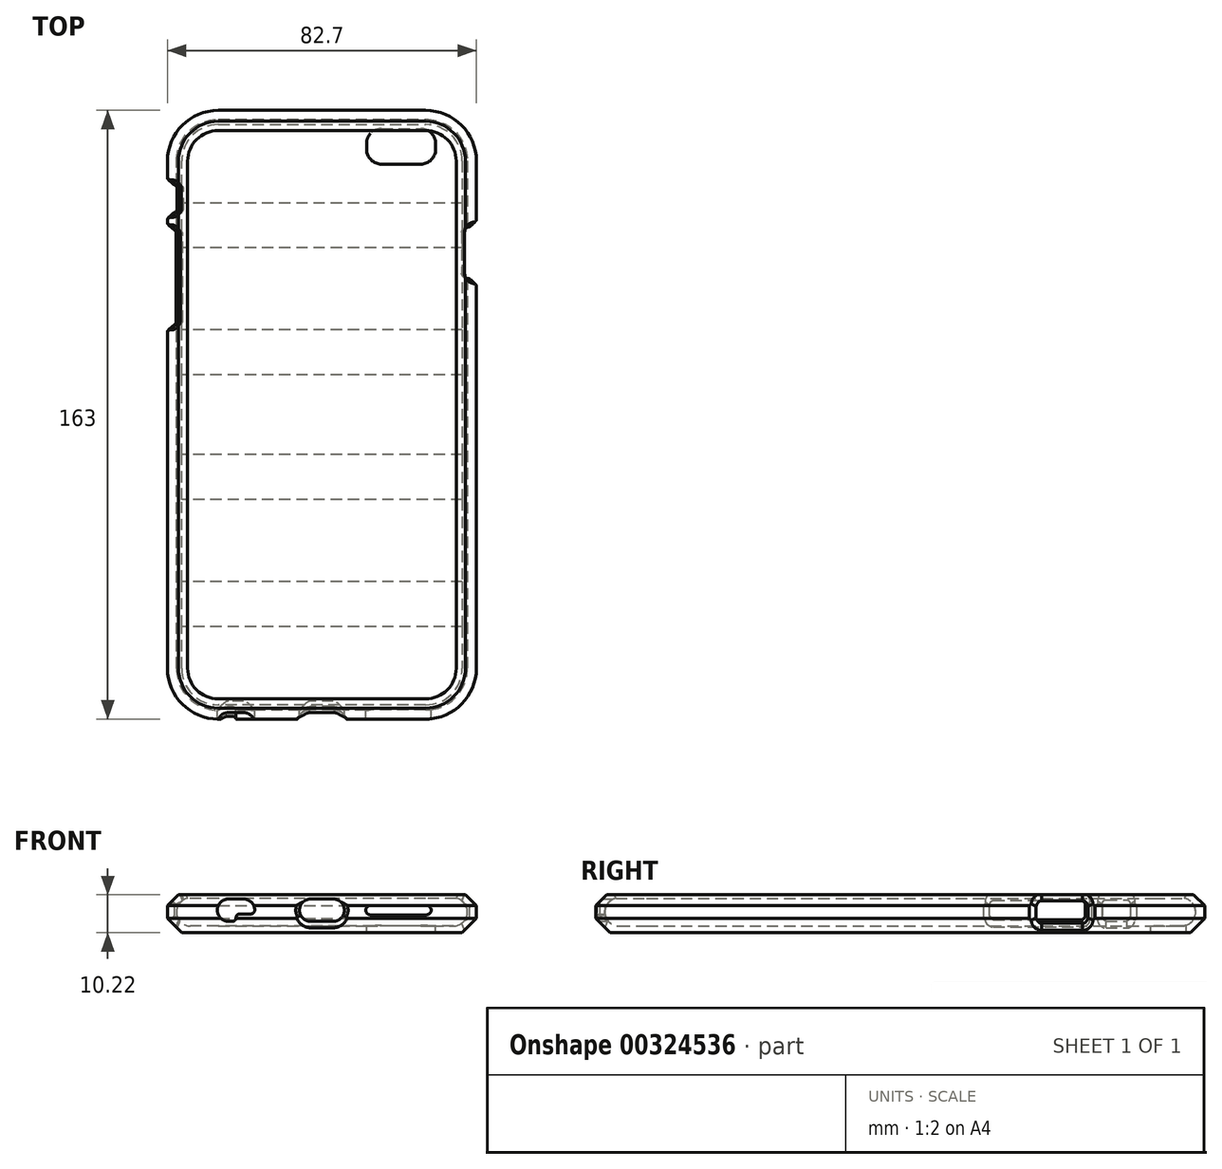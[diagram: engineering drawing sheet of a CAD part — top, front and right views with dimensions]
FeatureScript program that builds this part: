
annotation { "Feature Type Name" : "Feature", "Feature Type Description" : "" }
export const myFeature = defineFeature(function(context is Context, id is Id, definition is map)
    precondition{}
    {
        {
            assignVariable(context, id + "F0", {"name" : "HoleChamferLength", "anyValue" : 1.25});
        }
        {
            assignVariable(context, id + "F1", {"name" : "HoleChamferTopBottom", "anyValue" : 1.75});
        }
        {
            var Q0;
            Q0=qCreatedBy(makeId("Top.planeOp"),FACE);
            var sketch = newSketch(context, id + "F2", { "sketchPlane" : qUnion([Q0])});
            skLineSegment(sketch, "E0.bottom", {"start": v(27.75, 79.1) * mm, "end": v(0, 79.1) * mm});
            skLineSegment(sketch, "E0.top", {"start": v(27.75, -79.1) * mm, "end": v(-27.75, -79.1) * mm});
            skLineSegment(sketch, "E0.left", {"start": v(38.95, 67.9) * mm, "end": v(38.95, -67.9) * mm});
            skLineSegment(sketch, "E0.right", {"start": v(-38.95, 67.9) * mm, "end": v(-38.95, -67.9) * mm});
            skPoint(sketch, "E0.middle", {"position": v(0, 0) * mm});
            skPoint(sketch, "E1.visualSharp", {"position": v(-38.95, 79.1) * mm});
            skArc(sketch, "E1.filletArc", {"start": v(-27.75, 79.1) * mm, "mid": v(-35.67, 75.82) * mm, "end": v(-38.95, 67.9) * mm});
            skPoint(sketch, "E2.visualSharp", {"position": v(38.95, 79.1) * mm});
            skArc(sketch, "E2.filletArc", {"start": v(38.95, 67.9) * mm, "mid": v(35.67, 75.82) * mm, "end": v(27.75, 79.1) * mm});
            skPoint(sketch, "E3.visualSharp", {"position": v(38.95, -79.1) * mm});
            skArc(sketch, "E3.filletArc", {"start": v(27.75, -79.1) * mm, "mid": v(35.67, -75.82) * mm, "end": v(38.95, -67.9) * mm});
            skPoint(sketch, "E4.visualSharp", {"position": v(-38.95, -79.1) * mm});
            skArc(sketch, "E4.filletArc", {"start": v(-38.95, -67.9) * mm, "mid": v(-35.67, -75.82) * mm, "end": v(-27.75, -79.1) * mm});
            skLineSegment(sketch, "E5", {"start": v(0, 79.1) * mm, "end": v(-27.75, 79.1) * mm});
            skSolve(sketch);
        }
        {
            var Q0;
            Q0=qCreatedBy(makeId("Right.planeOp"),FACE);
            var sketch = newSketch(context, id + "F3", { "sketchPlane" : qUnion([Q0])});
            skPoint(sketch, "E6.0", {"position": v(79.1, 0) * mm});
            skArc(sketch, "E7", {"start": v(75.35, -3.75) * mm, "mid": v(79.1, 0) * mm, "end": v(75.35, 3.75) * mm});
            skLineSegment(sketch, "E8", {"start": v(75.35, -3.75) * mm, "end": v(75.35, 3.75) * mm, "construction": true});
            skLineSegment(sketch, "E9", {"start": v(81.5, -1.75) * mm, "end": v(81.5, 1.75) * mm});
            skLineSegment(sketch, "E10", {"start": v(81.5, 1.75) * mm, "end": v(79.75, 3.5) * mm});
            skLineSegment(sketch, "E11.trimOffspring", {"start": v(79.75, -3.5) * mm, "end": v(81.5, -1.75) * mm});
            skLineSegment(sketch, "E12", {"start": v(75.35, -5.55) * mm, "end": v(75.35, -3.75) * mm});
            skLineSegment(sketch, "E13", {"start": v(75.35, -5.55) * mm, "end": v(84.8, -5.55) * mm, "construction": true});
            skPoint(sketch, "E14", {"position": v(81.5, 0) * mm});
            skPoint(sketch, "E15.visualSharp", {"position": v(66.64, 4.7) * mm});
            skArc(sketch, "E15.filletArc", {"start": v(77.32, 4.67) * mm, "mid": v(76.53, 4.4) * mm, "end": v(76.1, 3.67) * mm});
            skLineSegment(sketch, "E16", {"start": v(79.75, -3.5) * mm, "end": v(77.7, -5.55) * mm});
            skLineSegment(sketch, "E17", {"start": v(77.7, -5.55) * mm, "end": v(75.35, -5.55) * mm});
            skLineSegment(sketch, "E18", {"start": v(79.75, 3.5) * mm, "end": v(78.58, 4.67) * mm});
            skLineSegment(sketch, "E19", {"start": v(78.58, 4.67) * mm, "end": v(77.32, 4.67) * mm});
            skLineSegment(sketch, "E20", {"start": v(76.1, 3.67) * mm, "end": v(66.64, 5.6) * mm, "construction": true});
            skSolve(sketch);
        }
        {
            var Q0;
            Q0=sQuery(id+"F2.wireOp",EDGE,"E5");
            var Q1;
            Q1=sQuery(id+"F2.wireOp",VERTEX,"E5.end");
            cPlane(context, id + "F4", {"entities" : qUnion([Q0, Q1]), "cplaneType" : CPlaneType.LINE_POINT, "offset" : 25 * mm, "width" : 150 * mm, "height" : 150 * mm});
        }
        {
            var Q0;
            Q0=sQuery(id+"F2.wireOp",EDGE,"E0.bottom");
            var Q1;
            Q1=sQuery(id+"F2.wireOp",VERTEX,"E2.filletArc.end");
            cPlane(context, id + "F5", {"entities" : qUnion([Q0, Q1]), "cplaneType" : CPlaneType.LINE_POINT, "offset" : 25 * mm, "width" : 150 * mm, "height" : 150 * mm});
        }
        {
            var Q0;
            Q0=sQuery(id+"F2.wireOp",EDGE,"E0.right");
            var Q1;
            Q1=sQuery(id+"F2.wireOp",VERTEX,"E0.right.end");
            cPlane(context, id + "F6", {"entities" : qUnion([Q0, Q1]), "cplaneType" : CPlaneType.LINE_POINT, "offset" : 25 * mm, "width" : 150 * mm, "height" : 150 * mm});
        }
        {
            var Q0;
            Q0=qCreatedBy(id+"F4.planeOp",FACE);
            var sketch = newSketch(context, id + "F7", { "sketchPlane" : qUnion([Q0])});
            skLineSegment(sketch, "E21.bottom", {"start": v(-24.95, -1.88) * mm, "end": v(-48.6, -1.88) * mm});
            skLineSegment(sketch, "E21.top", {"start": v(-24.95, 2.87) * mm, "end": v(-48.6, 2.87) * mm});
            skLineSegment(sketch, "E21.left", {"start": v(-23.95, -0.88) * mm, "end": v(-23.95, 1.87) * mm});
            skLineSegment(sketch, "E21.right", {"start": v(-49.6, -0.88) * mm, "end": v(-49.6, 1.87) * mm});
            skPoint(sketch, "E21.middle", {"position": v(-36.77, 0.5) * mm});
            skPoint(sketch, "E22.visualSharp", {"position": v(-49.6, 2.87) * mm});
            skArc(sketch, "E22.filletArc", {"start": v(-48.6, 2.87) * mm, "mid": v(-49.3, 2.58) * mm, "end": v(-49.6, 1.87) * mm});
            skPoint(sketch, "E23.visualSharp", {"position": v(-49.6, -1.88) * mm});
            skArc(sketch, "E23.filletArc", {"start": v(-49.6, -0.88) * mm, "mid": v(-49.3, -1.58) * mm, "end": v(-48.6, -1.88) * mm});
            skPoint(sketch, "E24.visualSharp", {"position": v(-23.95, 2.87) * mm});
            skArc(sketch, "E24.filletArc", {"start": v(-23.95, 1.87) * mm, "mid": v(-24.24, 2.58) * mm, "end": v(-24.95, 2.87) * mm});
            skPoint(sketch, "E25.visualSharp", {"position": v(-23.95, -1.88) * mm});
            skArc(sketch, "E25.filletArc", {"start": v(-24.95, -1.88) * mm, "mid": v(-24.24, -1.58) * mm, "end": v(-23.95, -0.88) * mm});
            skLineSegment(sketch, "E26.bottom", {"start": v(-60.6, 3.12) * mm, "end": v(-55.1, 3.12) * mm});
            skLineSegment(sketch, "E26.top", {"start": v(-60.6, -2.13) * mm, "end": v(-55.1, -2.13) * mm});
            skLineSegment(sketch, "E26.left", {"start": v(-61.6, 2.12) * mm, "end": v(-61.6, -1.13) * mm});
            skLineSegment(sketch, "E26.right", {"start": v(-54.1, 2.12) * mm, "end": v(-54.1, -1.13) * mm});
            skPoint(sketch, "E26.middle", {"position": v(-57.85, 0.5) * mm});
            skPoint(sketch, "E27.visualSharp", {"position": v(-61.6, 3.12) * mm});
            skArc(sketch, "E27.filletArc", {"start": v(-60.6, 3.13) * mm, "mid": v(-61.3, 2.83) * mm, "end": v(-61.6, 2.12) * mm});
            skPoint(sketch, "E28.visualSharp", {"position": v(-61.6, -2.13) * mm});
            skArc(sketch, "E28.filletArc", {"start": v(-61.6, -1.13) * mm, "mid": v(-61.3, -1.83) * mm, "end": v(-60.6, -2.13) * mm});
            skPoint(sketch, "E29.visualSharp", {"position": v(-54.1, -2.13) * mm});
            skArc(sketch, "E29.filletArc", {"start": v(-55.1, -2.13) * mm, "mid": v(-54.4, -1.83) * mm, "end": v(-54.1, -1.13) * mm});
            skPoint(sketch, "E30.visualSharp", {"position": v(-54.1, 3.12) * mm});
            skArc(sketch, "E30.filletArc", {"start": v(-54.1, 2.12) * mm, "mid": v(-54.4, 2.83) * mm, "end": v(-55.1, 3.13) * mm});
            skSolve(sketch);
        }
        {
            var Q0;
            Q0=qCreatedBy(id+"F5.planeOp",FACE);
            var sketch = newSketch(context, id + "F8", { "sketchPlane" : qUnion([Q0])});
            skLineSegment(sketch, "E31.bottom", {"start": v(-48.85, 2.75) * mm, "end": v(-37.85, 2.75) * mm});
            skLineSegment(sketch, "E31.top", {"start": v(-48.85, -2.75) * mm, "end": v(-37.85, -2.75) * mm});
            skLineSegment(sketch, "E31.left", {"start": v(-50.35, 1.25) * mm, "end": v(-50.35, -1.25) * mm});
            skLineSegment(sketch, "E31.right", {"start": v(-36.35, 1.25) * mm, "end": v(-36.35, -1.25) * mm});
            skPoint(sketch, "E31.middle", {"position": v(-43.35, 0) * mm});
            skPoint(sketch, "E32.visualSharp", {"position": v(-50.35, 2.75) * mm});
            skArc(sketch, "E32.filletArc", {"start": v(-48.85, 2.75) * mm, "mid": v(-49.91, 2.31) * mm, "end": v(-50.35, 1.25) * mm});
            skPoint(sketch, "E33.visualSharp", {"position": v(-50.35, -2.75) * mm});
            skArc(sketch, "E33.filletArc", {"start": v(-50.35, -1.25) * mm, "mid": v(-49.91, -2.31) * mm, "end": v(-48.85, -2.75) * mm});
            skPoint(sketch, "E34.visualSharp", {"position": v(-36.35, -2.75) * mm});
            skArc(sketch, "E34.filletArc", {"start": v(-37.85, -2.75) * mm, "mid": v(-36.79, -2.31) * mm, "end": v(-36.35, -1.25) * mm});
            skPoint(sketch, "E35.visualSharp", {"position": v(-36.35, 2.75) * mm});
            skArc(sketch, "E35.filletArc", {"start": v(-36.35, 1.25) * mm, "mid": v(-36.79, 2.31) * mm, "end": v(-37.85, 2.75) * mm});
            skSolve(sketch);
        }
        {
            var Q0;
            Q0=qCreatedBy(id+"F6.planeOp",FACE);
            var sketch = newSketch(context, id + "F9", { "sketchPlane" : qUnion([Q0])});
            skLineSegment(sketch, "E36.bottom", {"start": v(3, 3.5) * mm, "end": v(-3, 3.5) * mm});
            skLineSegment(sketch, "E36.top", {"start": v(3, -2.5) * mm, "end": v(-3, -2.5) * mm});
            skLineSegment(sketch, "E36.left", {"start": v(6, 0.5) * mm, "end": v(6, 0.5) * mm});
            skLineSegment(sketch, "E36.right", {"start": v(-6, 0.5) * mm, "end": v(-6, 0.5) * mm});
            skPoint(sketch, "E36.middle", {"position": v(0, 0.5) * mm});
            skArc(sketch, "E37", {"start": v(-25, 3.5) * mm, "mid": v(-28, 0.5) * mm, "end": v(-25, -2.5) * mm});
            skPoint(sketch, "E38.visualSharp", {"position": v(-6, 3.5) * mm});
            skArc(sketch, "E38.filletArc", {"start": v(-3, 3.5) * mm, "mid": v(-5.12, 2.62) * mm, "end": v(-6, 0.5) * mm});
            skPoint(sketch, "E39.visualSharp", {"position": v(-6, -2.5) * mm});
            skArc(sketch, "E39.filletArc", {"start": v(-6, 0.5) * mm, "mid": v(-5.12, -1.62) * mm, "end": v(-3, -2.5) * mm});
            skPoint(sketch, "E40.visualSharp", {"position": v(6, -2.5) * mm});
            skArc(sketch, "E40.filletArc", {"start": v(3, -2.5) * mm, "mid": v(5.12, -1.62) * mm, "end": v(6, 0.5) * mm});
            skPoint(sketch, "E41.visualSharp", {"position": v(6, 3.5) * mm});
            skArc(sketch, "E41.filletArc", {"start": v(6, 0.5) * mm, "mid": v(5.12, 2.62) * mm, "end": v(3, 3.5) * mm});
            skArc(sketch, "E42", {"start": v(-21, -2.5) * mm, "mid": v(-19.27, -1.95) * mm, "end": v(-18.17, -0.5) * mm, "construction": true});
            skLineSegment(sketch, "E43", {"start": v(-21, 3.5) * mm, "end": v(-25, 3.5) * mm});
            skLineSegment(sketch, "E44", {"start": v(-21, -2.5) * mm, "end": v(-23, -2.5) * mm, "construction": true});
            skLineSegment(sketch, "E45", {"start": v(13, 0.5) * mm, "end": v(28, 0.5) * mm, "construction": true});
            skArc(sketch, "E46.0.startCap", {"start": v(13, -0.75) * mm, "mid": v(11.75, 0.5) * mm, "end": v(13, 1.75) * mm});
            skArc(sketch, "E46.0.endCap", {"start": v(28, 1.75) * mm, "mid": v(29.25, 0.5) * mm, "end": v(28, -0.75) * mm});
            skLineSegment(sketch, "E46.0.left", {"start": v(13, 1.75) * mm, "end": v(28, 1.75) * mm});
            skLineSegment(sketch, "E46.0.right", {"start": v(13, -0.75) * mm, "end": v(28, -0.75) * mm});
            skLineSegment(sketch, "E47", {"start": v(-23, -1.5) * mm, "end": v(-23, -1.5) * mm});
            skLineSegment(sketch, "E48", {"start": v(-22, -0.5) * mm, "end": v(-19, -0.5) * mm});
            skLineSegment(sketch, "E49", {"start": v(-24, -2.5) * mm, "end": v(-25, -2.5) * mm});
            skArc(sketch, "E50", {"start": v(-18, 0.5) * mm, "mid": v(-18.88, 2.62) * mm, "end": v(-21, 3.5) * mm});
            skPoint(sketch, "E51.visualSharp", {"position": v(-23, -0.5) * mm});
            skArc(sketch, "E51.filletArc", {"start": v(-22, -0.5) * mm, "mid": v(-22.7, -0.8) * mm, "end": v(-23, -1.5) * mm});
            skPoint(sketch, "E52.visualSharp", {"position": v(-23, -2.5) * mm});
            skArc(sketch, "E52.filletArc", {"start": v(-24, -2.5) * mm, "mid": v(-23.3, -2.2) * mm, "end": v(-23, -1.5) * mm});
            skPoint(sketch, "E53.visualSharp", {"position": v(-18.17, -0.5) * mm});
            skArc(sketch, "E53.filletArc", {"start": v(-19, -0.5) * mm, "mid": v(-18.3, -0.2) * mm, "end": v(-18, 0.5) * mm});
            skCircle(sketch, "E54", {"center": v(-25, 0.5) * mm, "radius": 2.5 * mm, "construction": true});
            skSolve(sketch);
        }
        {
            var Q0;
            Q0=qCreatedBy(makeId("Top.planeOp"),FACE);
            var sketch = newSketch(context, id + "F10", { "sketchPlane" : qUnion([Q0])});
            skLineSegment(sketch, "E55.bottom", {"start": v(26.45, 67.1) * mm, "end": v(15.95, 67.1) * mm});
            skLineSegment(sketch, "E55.top", {"start": v(26.45, 76.6) * mm, "end": v(15.95, 76.6) * mm});
            skLineSegment(sketch, "E55.left", {"start": v(30.45, 71.1) * mm, "end": v(30.45, 72.6) * mm});
            skLineSegment(sketch, "E55.right", {"start": v(11.95, 71.1) * mm, "end": v(11.95, 72.6) * mm});
            skPoint(sketch, "E55.middle", {"position": v(21.2, 71.85) * mm});
            skPoint(sketch, "E56.visualSharp", {"position": v(11.95, 76.6) * mm});
            skArc(sketch, "E56.filletArc", {"start": v(15.95, 76.6) * mm, "mid": v(13.12, 75.43) * mm, "end": v(11.95, 72.6) * mm});
            skPoint(sketch, "E57.visualSharp", {"position": v(11.95, 67.1) * mm});
            skArc(sketch, "E57.filletArc", {"start": v(11.95, 71.1) * mm, "mid": v(13.12, 68.27) * mm, "end": v(15.95, 67.1) * mm});
            skPoint(sketch, "E58.visualSharp", {"position": v(30.45, 67.1) * mm});
            skArc(sketch, "E58.filletArc", {"start": v(26.45, 67.1) * mm, "mid": v(29.28, 68.27) * mm, "end": v(30.45, 71.1) * mm});
            skPoint(sketch, "E59.visualSharp", {"position": v(30.45, 76.6) * mm});
            skArc(sketch, "E59.filletArc", {"start": v(30.45, 72.6) * mm, "mid": v(29.28, 75.43) * mm, "end": v(26.45, 76.6) * mm});
            skSolve(sketch);
        }
        {
            var Q0;
            Q0=qSketchRegion(id+"F3",true);
            var Q1;
            Q1=sQuery(id+"F2.wireOp",EDGE,"E5");
            var Q2;
            Q2=sQuery(id+"F2.wireOp",EDGE,"E1.filletArc");
            var Q3;
            Q3=sQuery(id+"F2.wireOp",EDGE,"E0.right");
            var Q4;
            Q4=sQuery(id+"F2.wireOp",EDGE,"E4.filletArc");
            var Q5;
            Q5=sQuery(id+"F2.wireOp",EDGE,"E0.top");
            var Q6;
            Q6=sQuery(id+"F2.wireOp",EDGE,"E3.filletArc");
            var Q7;
            Q7=sQuery(id+"F2.wireOp",EDGE,"E0.left");
            var Q8;
            Q8=sQuery(id+"F2.wireOp",EDGE,"E2.filletArc");
            var Q9;
            Q9=sQuery(id+"F2.wireOp",EDGE,"E0.bottom");
            sweep(context, id + "F11", {"profiles" : qUnion([Q0]), "path" : qUnion([Q1, Q2, Q3, Q4, Q5, Q6, Q7, Q8, Q9])});
        }
        {
            var Q0;
            Q0=qCreatedBy(makeId("Front.planeOp"),FACE);
            var sketch = newSketch(context, id + "F12", { "sketchPlane" : qUnion([Q0])});
            skLineSegment(sketch, "E60.0.0", {"start": v(35.2, -5.55) * mm, "end": v(27.75, -5.55) * mm});
            skLineSegment(sketch, "E60.0.1", {"start": v(27.75, -3.75) * mm, "end": v(27.75, -5.55) * mm});
            skLineSegment(sketch, "E60.0.2", {"start": v(27.75, -3.75) * mm, "end": v(35.2, -3.75) * mm});
            skLineSegment(sketch, "E60.0.3", {"start": v(35.2, -3.75) * mm, "end": v(35.2, -5.55) * mm});
            skLineSegment(sketch, "E60.1.0", {"start": v(27.75, -5.55) * mm, "end": v(-27.75, -5.55) * mm});
            skLineSegment(sketch, "E60.1.1", {"start": v(-27.75, -3.75) * mm, "end": v(-27.75, -5.55) * mm});
            skLineSegment(sketch, "E60.1.2", {"start": v(-27.75, -3.75) * mm, "end": v(27.75, -3.75) * mm});
            skLineSegment(sketch, "E60.1.3", {"start": v(27.75, -3.75) * mm, "end": v(27.75, -5.55) * mm});
            skLineSegment(sketch, "E60.2.0", {"start": v(-27.75, -5.55) * mm, "end": v(-35.2, -5.55) * mm});
            skLineSegment(sketch, "E60.2.1", {"start": v(-35.2, -3.75) * mm, "end": v(-35.2, -5.55) * mm});
            skLineSegment(sketch, "E60.2.2", {"start": v(-35.2, -3.75) * mm, "end": v(-27.75, -3.75) * mm});
            skLineSegment(sketch, "E60.2.3", {"start": v(-27.75, -3.75) * mm, "end": v(-27.75, -5.55) * mm});
            skSolve(sketch);
        }
        {
            var Q0;
            Q0=qSketchRegion(id+"F12",true);
            extrude(context, id + "F13", {"entities" : qUnion([Q0]), "operationType" : NewBodyOperationType.ADD, "endBound" : BoundingType.UP_TO_NEXT, "depth" : 25 * mm, "hasSecondDirection" : true, "secondDirectionBound" : SecondDirectionBoundingType.UP_TO_NEXT, "secondDirectionOppositeDirection" : true, "secondDirectionDepth" : 25 * mm});
        }
        {
            var Q0;
            Q0=qSketchRegion(id+"F7",true);
            extrude(context, id + "F14", {"entities" : qUnion([Q0]), "operationType" : NewBodyOperationType.REMOVE, "endBound" : BoundingType.THROUGH_ALL, "depth" : 25 * mm});
        }
        {
            var Q0;
            Q0=qSketchRegion(id+"F8",true);
            extrude(context, id + "F15", {"entities" : qUnion([Q0]), "operationType" : NewBodyOperationType.REMOVE, "endBound" : BoundingType.THROUGH_ALL, "oppositeDirection" : true, "depth" : 25 * mm});
        }
        {
            var Q0;
            Q0=makeQuery(id+"F10.imprint","IMPRINT",FACE,{"disambiguationData":[TD([[makeQuery(id+"F10.imprint","IMPRINT",EDGE,{"derivedFrom":sQuery(id+"F10.wireOp",EDGE,"E55.bottom")}),-1.0]])]});
            extrude(context, id + "F16", {"entities" : qUnion([Q0]), "operationType" : NewBodyOperationType.REMOVE, "endBound" : BoundingType.THROUGH_ALL, "oppositeDirection" : true, "depth" : 25 * mm});
        }
        {
            var Q0;
            Q0=qSketchRegion(id+"F9",true);
            extrude(context, id + "F17", {"entities" : qUnion([Q0]), "operationType" : NewBodyOperationType.REMOVE, "endBound" : BoundingType.THROUGH_ALL, "depth" : 25 * mm});
        }
        {
            var Q0;
            Q0=makeQuery(id+"F14.boolean.opBoolean","INTERSECT",EDGE,{"derivedFrom":[makeQuery(id+"F11.opSweep","SWEPT_FACE",FACE,{"disambiguationData":[OSD([sQuery(id+"F2.wireOp",EDGE,"E0.right"),sQuery(id+"F3.wireOp",EDGE,"E11.trimOffspring"),sQuery(id+"F3.wireOp",EDGE,"E16")])]}),makeQuery(id+"F14.opExtrude","SWEPT_FACE",FACE,{"disambiguationData":[OSD([sQuery(id+"F7.wireOp",EDGE,"E21.bottom")])]})]});
            var Q1;
            Q1=makeQuery(id+"F14.boolean.opBoolean","INTERSECT",EDGE,{"derivedFrom":[makeQuery(id+"F11.opSweep","SWEPT_FACE",FACE,{"disambiguationData":[OSD([sQuery(id+"F2.wireOp",EDGE,"E0.right"),sQuery(id+"F3.wireOp",EDGE,"E10")])]}),makeQuery(id+"F14.opExtrude","SWEPT_FACE",FACE,{"disambiguationData":[OSD([sQuery(id+"F7.wireOp",EDGE,"E21.top")])]})]});
            chamfer(context, id + "F18", {"entities" : qUnion([Q0, Q1]), "width" : (getVariable(context, 'HoleChamferLength')) * mm, "tangentPropagation" : true});
        }
        {
            var Q0;
            Q0=makeQuery(id+"F14.boolean.opBoolean","INTERSECT",EDGE,{"derivedFrom":[makeQuery(id+"F11.opSweep","SWEPT_FACE",FACE,{"disambiguationData":[OSD([sQuery(id+"F2.wireOp",EDGE,"E0.right"),sQuery(id+"F3.wireOp",EDGE,"E11.trimOffspring"),sQuery(id+"F3.wireOp",EDGE,"E16")])]}),makeQuery(id+"F14.opExtrude","SWEPT_FACE",FACE,{"disambiguationData":[OSD([sQuery(id+"F7.wireOp",EDGE,"E26.top")])]})]});
            var Q1;
            Q1=makeQuery(id+"F14.boolean.opBoolean","INTERSECT",EDGE,{"derivedFrom":[makeQuery(id+"F11.opSweep","SWEPT_FACE",FACE,{"disambiguationData":[OSD([sQuery(id+"F2.wireOp",EDGE,"E0.right"),sQuery(id+"F3.wireOp",EDGE,"E10")])]}),makeQuery(id+"F14.opExtrude","SWEPT_FACE",FACE,{"disambiguationData":[OSD([sQuery(id+"F7.wireOp",EDGE,"E26.bottom")])]})]});
            chamfer(context, id + "F19", {"entities" : qUnion([Q0, Q1]), "width" : (getVariable(context, 'HoleChamferLength')) * mm, "tangentPropagation" : true});
        }
        {
            var Q0;
            Q0=makeQuery(id+"F15.boolean.opBoolean","INTERSECT",EDGE,{"derivedFrom":[makeQuery(id+"F11.opSweep","SWEPT_FACE",FACE,{"disambiguationData":[OSD([sQuery(id+"F2.wireOp",EDGE,"E0.left"),sQuery(id+"F3.wireOp",EDGE,"E11.trimOffspring"),sQuery(id+"F3.wireOp",EDGE,"E16")])]}),makeQuery(id+"F15.opExtrude","SWEPT_FACE",FACE,{"disambiguationData":[OSD([sQuery(id+"F8.wireOp",EDGE,"E31.top")])]})]});
            var Q1;
            Q1=makeQuery(id+"F15.boolean.opBoolean","INTERSECT",EDGE,{"derivedFrom":[makeQuery(id+"F11.opSweep","SWEPT_FACE",FACE,{"disambiguationData":[OSD([sQuery(id+"F2.wireOp",EDGE,"E0.left"),sQuery(id+"F3.wireOp",EDGE,"E10")])]}),makeQuery(id+"F15.opExtrude","SWEPT_FACE",FACE,{"disambiguationData":[OSD([sQuery(id+"F8.wireOp",EDGE,"E31.bottom")])]})]});
            chamfer(context, id + "F20", {"entities" : qUnion([Q0, Q1]), "width" : (getVariable(context, 'HoleChamferLength')) * mm, "tangentPropagation" : true});
        }
        {
            var Q0;
            Q0=makeQuery(id+"F15.boolean.opBoolean","INTERSECT",EDGE,{"derivedFrom":[makeQuery(id+"F11.opSweep","SWEPT_FACE",FACE,{"disambiguationData":[OSD([sQuery(id+"F2.wireOp",EDGE,"E0.left"),sQuery(id+"F3.wireOp",EDGE,"E9")])]}),makeQuery(id+"F15.opExtrude","SWEPT_FACE",FACE,{"disambiguationData":[OSD([sQuery(id+"F8.wireOp",EDGE,"E31.left")])]})]});
            var Q1;
            Q1=makeQuery(id+"F15.boolean.opBoolean","INTERSECT",EDGE,{"derivedFrom":[makeQuery(id+"F11.opSweep","SWEPT_FACE",FACE,{"disambiguationData":[OSD([sQuery(id+"F2.wireOp",EDGE,"E0.left"),sQuery(id+"F3.wireOp",EDGE,"E9")])]}),makeQuery(id+"F15.opExtrude","SWEPT_FACE",FACE,{"disambiguationData":[OSD([sQuery(id+"F8.wireOp",EDGE,"E31.right")])]})]});
            var Q2;
            Q2=makeQuery(id+"F14.boolean.opBoolean","INTERSECT",EDGE,{"derivedFrom":[makeQuery(id+"F11.opSweep","SWEPT_FACE",FACE,{"disambiguationData":[OSD([sQuery(id+"F2.wireOp",EDGE,"E0.right"),sQuery(id+"F3.wireOp",EDGE,"E9")])]}),makeQuery(id+"F14.opExtrude","SWEPT_FACE",FACE,{"disambiguationData":[OSD([sQuery(id+"F7.wireOp",EDGE,"E21.left")])]})]});
            var Q3;
            Q3=makeQuery(id+"F14.boolean.opBoolean","INTERSECT",EDGE,{"derivedFrom":[makeQuery(id+"F11.opSweep","SWEPT_FACE",FACE,{"disambiguationData":[OSD([sQuery(id+"F2.wireOp",EDGE,"E0.right"),sQuery(id+"F3.wireOp",EDGE,"E9")])]}),makeQuery(id+"F14.opExtrude","SWEPT_FACE",FACE,{"disambiguationData":[OSD([sQuery(id+"F7.wireOp",EDGE,"E21.right")])]})]});
            var Q4;
            Q4=makeQuery(id+"F14.boolean.opBoolean","INTERSECT",EDGE,{"derivedFrom":[makeQuery(id+"F11.opSweep","SWEPT_FACE",FACE,{"disambiguationData":[OSD([sQuery(id+"F2.wireOp",EDGE,"E0.right"),sQuery(id+"F3.wireOp",EDGE,"E9")])]}),makeQuery(id+"F14.opExtrude","SWEPT_FACE",FACE,{"disambiguationData":[OSD([sQuery(id+"F7.wireOp",EDGE,"E26.left")])]})]});
            var Q5;
            Q5=makeQuery(id+"F14.boolean.opBoolean","INTERSECT",EDGE,{"derivedFrom":[makeQuery(id+"F11.opSweep","SWEPT_FACE",FACE,{"disambiguationData":[OSD([sQuery(id+"F2.wireOp",EDGE,"E0.right"),sQuery(id+"F3.wireOp",EDGE,"E9")])]}),makeQuery(id+"F14.opExtrude","SWEPT_FACE",FACE,{"disambiguationData":[OSD([sQuery(id+"F7.wireOp",EDGE,"E26.right")])]})]});
            chamfer(context, id + "F21", {"entities" : qUnion([Q0, Q1, Q2, Q3, Q4, Q5]), "width" : (getVariable(context, 'HoleChamferTopBottom')) * mm, "tangentPropagation" : true});
        }
        {
            var Q0;
            Q0=makeQuery(id+"F17.boolean.opBoolean","INTERSECT",EDGE,{"derivedFrom":[makeQuery(id+"F11.opSweep","SWEPT_FACE",FACE,{"disambiguationData":[OSD([sQuery(id+"F2.wireOp",EDGE,"E0.top"),sQuery(id+"F3.wireOp",EDGE,"E11.trimOffspring"),sQuery(id+"F3.wireOp",EDGE,"E16")])]}),makeQuery(id+"F17.opExtrude","SWEPT_FACE",FACE,{"disambiguationData":[OSD([sQuery(id+"F9.wireOp",EDGE,"E36.top")])]})]});
            var Q1;
            Q1=makeQuery(id+"F17.boolean.opBoolean","INTERSECT",EDGE,{"derivedFrom":[makeQuery(id+"F11.opSweep","SWEPT_FACE",FACE,{"disambiguationData":[OSD([sQuery(id+"F2.wireOp",EDGE,"E0.top"),sQuery(id+"F3.wireOp",EDGE,"E9")])]}),makeQuery(id+"F17.opExtrude","SWEPT_FACE",FACE,{"disambiguationData":[OSD([sQuery(id+"F9.wireOp",EDGE,"E38.filletArc"),sQuery(id+"F9.wireOp",EDGE,"E39.filletArc")])]})]});
            var Q2;
            Q2=makeQuery(id+"F17.boolean.opBoolean","INTERSECT",EDGE,{"derivedFrom":[makeQuery(id+"F11.opSweep","SWEPT_FACE",FACE,{"disambiguationData":[OSD([sQuery(id+"F2.wireOp",EDGE,"E0.top"),sQuery(id+"F3.wireOp",EDGE,"E9")])]}),makeQuery(id+"F17.opExtrude","SWEPT_FACE",FACE,{"disambiguationData":[OSD([sQuery(id+"F9.wireOp",EDGE,"E40.filletArc"),sQuery(id+"F9.wireOp",EDGE,"E41.filletArc")])]})]});
            chamfer(context, id + "F22", {"entities" : qUnion([Q0, Q1, Q2]), "width" : 1 * mm, "tangentPropagation" : true});
        }
        {
            var Q0;
            Q0=qCreatedBy(makeId("Right.planeOp"),FACE);
            var sketch = newSketch(context, id + "F23", { "sketchPlane" : qUnion([Q0])});
            skLineSegment(sketch, "E61", {"start": v(73.83, -4.65) * mm, "end": v(73.23, -4.65) * mm});
            skLineSegment(sketch, "E62", {"start": v(72.71, -5.55) * mm, "end": v(74.35, -5.55) * mm});
            skLineSegment(sketch, "E63", {"start": v(74.35, -5.55) * mm, "end": v(73.83, -4.65) * mm});
            skLineSegment(sketch, "E64", {"start": v(73.23, -4.65) * mm, "end": v(72.71, -5.55) * mm});
            skSolve(sketch);
        }
        {
            var Q0;
            Q0=makeQuery(id+"F13.boolean.opBoolean","MERGE",FACE,{"derivedFrom":[makeQuery(id+"F11.opSweep","SWEPT_FACE",FACE,{"disambiguationData":[OSD([sQuery(id+"F2.wireOp",EDGE,"E0.bottom"),sQuery(id+"F3.wireOp",EDGE,"E17")])]}),makeQuery(id+"F13.opExtrude","SWEPT_FACE",FACE,{"disambiguationData":[OSD([sQuery(id+"F12.wireOp",EDGE,"E60.0.0"),sQuery(id+"F12.wireOp",EDGE,"E60.1.0"),sQuery(id+"F12.wireOp",EDGE,"E60.2.0")])]})]});
            var sketch = newSketch(context, id + "F24", { "sketchPlane" : qUnion([Q0])});
            skArc(sketch, "E65.0.0", {"start": v(-37.55, -67.9) * mm, "mid": v(-34.68, -74.83) * mm, "end": v(-27.75, -77.7) * mm});
            skLineSegment(sketch, "E65.0.1", {"start": v(-27.75, -77.7) * mm, "end": v(27.75, -77.7) * mm});
            skArc(sketch, "E65.0.2", {"start": v(27.75, -77.7) * mm, "mid": v(34.68, -74.83) * mm, "end": v(37.55, -67.9) * mm});
            skLineSegment(sketch, "E65.0.3", {"start": v(37.55, -67.9) * mm, "end": v(37.55, 67.9) * mm});
            skArc(sketch, "E65.0.4", {"start": v(37.55, 67.9) * mm, "mid": v(34.68, 74.83) * mm, "end": v(27.75, 77.7) * mm});
            skLineSegment(sketch, "E65.0.5", {"start": v(27.75, 77.7) * mm, "end": v(-27.75, 77.7) * mm});
            skArc(sketch, "E65.0.6", {"start": v(-27.75, 77.7) * mm, "mid": v(-34.68, 74.83) * mm, "end": v(-37.55, 67.9) * mm});
            skLineSegment(sketch, "E65.0.7", {"start": v(-37.55, 67.9) * mm, "end": v(-37.55, -67.9) * mm});
            skPoint(sketch, "E66.0", {"position": v(13.12, -75.43) * mm});
            skPoint(sketch, "E67.0", {"position": v(11.95, -72.6) * mm});
            skPoint(sketch, "E68.0", {"position": v(13.12, -68.27) * mm});
            skPoint(sketch, "E69.0", {"position": v(29.28, -68.27) * mm});
            skArc(sketch, "E70.0", {"start": v(15.95, -67.1) * mm, "mid": v(13.12, -68.27) * mm, "end": v(11.95, -71.1) * mm});
            skArc(sketch, "E71.0", {"start": v(11.95, -72.6) * mm, "mid": v(13.12, -75.43) * mm, "end": v(15.95, -76.6) * mm});
            skLineSegment(sketch, "E72.0", {"start": v(15.95, -76.6) * mm, "end": v(26.45, -76.6) * mm});
            skArc(sketch, "E73.0", {"start": v(26.45, -76.6) * mm, "mid": v(29.28, -75.43) * mm, "end": v(30.45, -72.6) * mm});
            skPoint(sketch, "E74.0", {"position": v(21.2, -67.1) * mm});
            skLineSegment(sketch, "E75", {"start": v(37.55, -56.7) * mm, "end": v(-37.55, -56.7) * mm});
            skLineSegment(sketch, "E76", {"start": v(37.55, -44.7) * mm, "end": v(-37.55, -44.7) * mm});
            skLineSegment(sketch, "E77", {"start": v(37.55, -22.7) * mm, "end": v(-37.55, -22.7) * mm});
            skLineSegment(sketch, "E78", {"start": v(37.55, -10.7) * mm, "end": v(-37.55, -10.7) * mm});
            skLineSegment(sketch, "E79", {"start": v(37.55, 10.7) * mm, "end": v(-37.55, 10.7) * mm});
            skLineSegment(sketch, "E80", {"start": v(37.55, 22.7) * mm, "end": v(-37.55, 22.7) * mm});
            skLineSegment(sketch, "E81", {"start": v(37.55, 44.7) * mm, "end": v(-37.55, 44.7) * mm});
            skLineSegment(sketch, "E82", {"start": v(37.55, 56.7) * mm, "end": v(-37.55, 56.7) * mm});
            skSolve(sketch);
        }
        {
            var Q0;
            {var subQ0=sQuery(id+"F24.wireOp",EDGE,"E81");Q0=makeQuery(id+"F24.imprint","IMPRINT",FACE,{"disambiguationData":[TD([[makeQuery(id+"F24.imprint","IMPRINT",EDGE,{"derivedFrom":subQ0}),-1.0]])]});}
            var Q1;
            {var subQ0=sQuery(id+"F24.wireOp",EDGE,"E79");Q1=makeQuery(id+"F24.imprint","IMPRINT",FACE,{"disambiguationData":[TD([[makeQuery(id+"F24.imprint","IMPRINT",EDGE,{"derivedFrom":subQ0}),-1.0]])]});}
            var Q2;
            {var subQ0=sQuery(id+"F24.wireOp",EDGE,"E77");Q2=makeQuery(id+"F24.imprint","IMPRINT",FACE,{"disambiguationData":[TD([[makeQuery(id+"F24.imprint","IMPRINT",EDGE,{"derivedFrom":subQ0}),-1.0]])]});}
            var Q3;
            {var subQ0=sQuery(id+"F24.wireOp",EDGE,"E75");Q3=makeQuery(id+"F24.imprint","IMPRINT",FACE,{"disambiguationData":[TD([[makeQuery(id+"F24.imprint","IMPRINT",EDGE,{"derivedFrom":subQ0}),-1.0]])]});}
            extrude(context, id + "F25", {"entities" : qUnion([Q0, Q1, Q2, Q3]), "operationType" : NewBodyOperationType.REMOVE, "oppositeDirection" : true, "depth" : .2 * mm});
        }
    });
